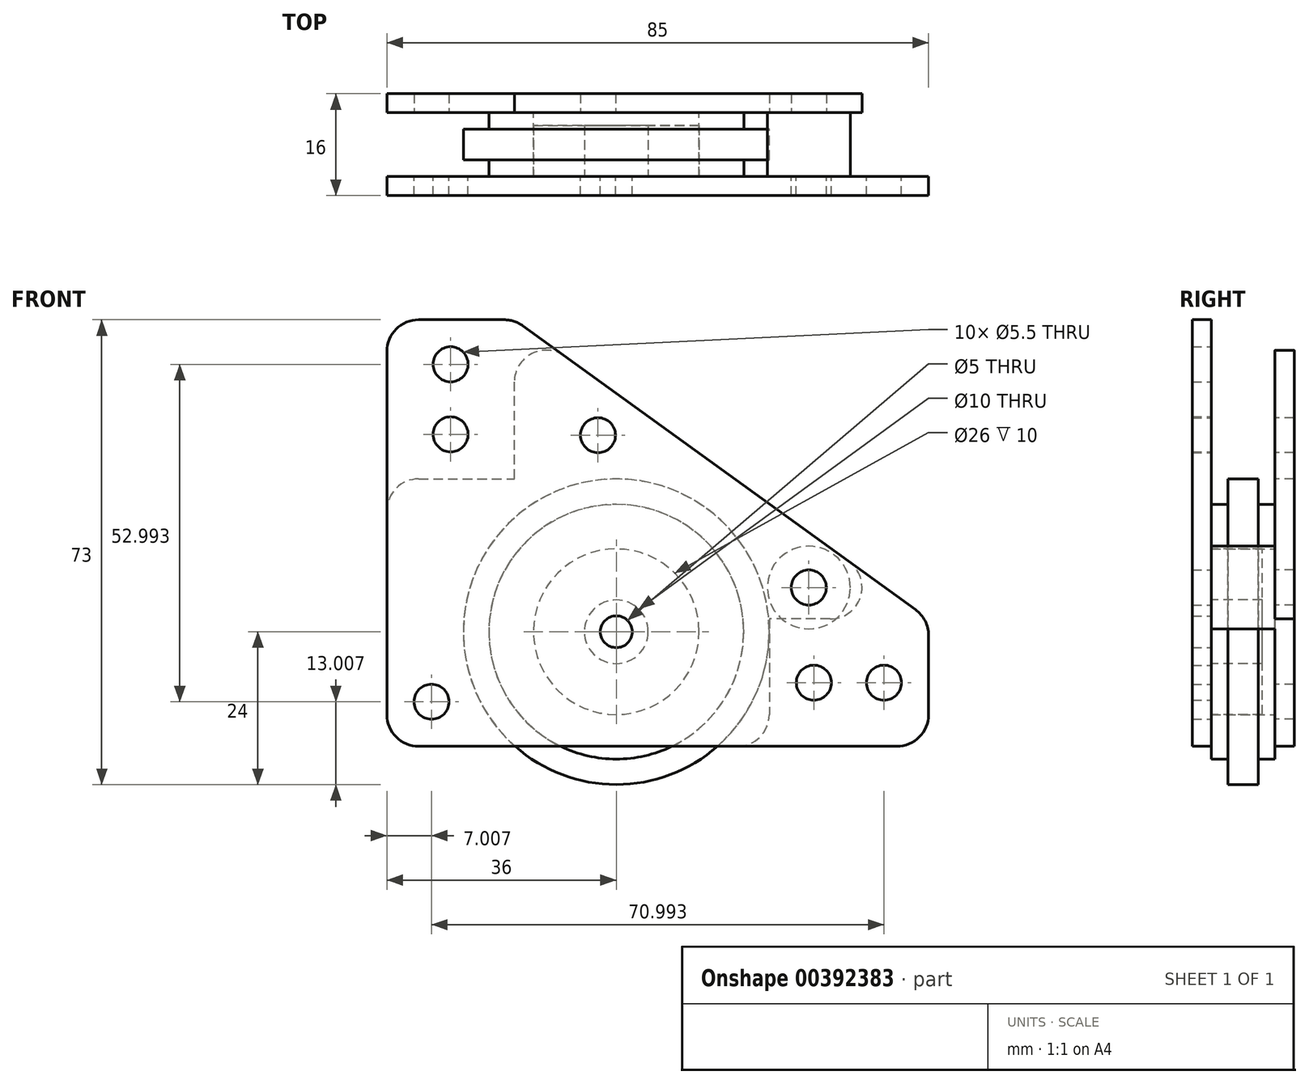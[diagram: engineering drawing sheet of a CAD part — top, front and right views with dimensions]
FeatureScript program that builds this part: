
annotation { "Feature Type Name" : "Feature", "Feature Type Description" : "" }
export const myFeature = defineFeature(function(context is Context, id is Id, definition is map)
    precondition{}
    {
        {
            var Q0;
            Q0=qCreatedBy(makeId("Front.planeOp"),FACE);
            var sketch = newSketch(context, id + "F0", { "sketchPlane" : qUnion([Q0])});
            skCircle(sketch, "E0", {"center": v(0, 0) * mm, "radius": 20 * mm});
            skCircle(sketch, "E1", {"center": v(0, 0) * mm, "radius": 24 * mm});
            skCircle(sketch, "E2", {"center": v(0, 0) * mm, "radius": 13 * mm});
            skSolve(sketch);
        }
        {
            var Q0;
            Q0=makeQuery(id+"F0.imprint","IMPRINT",FACE,{"disambiguationData":[TD([[makeQuery(id+"F0.imprint","IMPRINT",EDGE,{"derivedFrom":sQuery(id+"F0.wireOp",EDGE,"E0")}),1.0]])]});
            var Q1;
            Q1=makeQuery(id+"F0.imprint","IMPRINT",FACE,{"disambiguationData":[TD([[makeQuery(id+"F0.imprint","IMPRINT",EDGE,{"derivedFrom":sQuery(id+"F0.wireOp",EDGE,"E2")}),-1.0]])]});
            var Q2;
            Q2=makeQuery(id+"F0.imprint","IMPRINT",FACE,{"disambiguationData":[TD([[makeQuery(id+"F0.imprint","IMPRINT",EDGE,{"derivedFrom":sQuery(id+"F0.wireOp",EDGE,"ffxK04Et-xQjH-tJyI-gLSu-BGhigi1zAa47")}),-1.0]])]});
            extrude(context, id + "F1", {"entities" : qUnion([Q0, Q1, Q2]), "endBound" : BoundingType.SYMMETRIC, "depth" : 10 * mm});
        }
        {
            var Q0;
            Q0 = qSketchRegion(id + "F0", true);
            extrude(context, id + "F2", {"entities" : qUnion([Q0]), "operationType" : NewBodyOperationType.ADD, "endBound" : BoundingType.SYMMETRIC, "depth" : 4.8 * mm});
        }
        {
            var Q0;
            Q0=makeQuery(id+"F1.opExtrude","CAP_FACE",FACE,{"disambiguationData":[OSD([sQuery(id+"F0.wireOp",EDGE,"E0"),sQuery(id+"F0.wireOp",EDGE,"E2")])],"isStart":false});
            cPlane(context, id + "F3", {"entities" : qUnion([Q0]), "cplaneType" : CPlaneType.OFFSET, "offset" : 0 * mm, "width" : 150 * mm, "height" : 150 * mm});
        }
        {
            var Q0;
            Q0=qCreatedBy(id+"F3.planeOp",FACE);
            var sketch = newSketch(context, id + "F4", { "sketchPlane" : qUnion([Q0])});
            skLineSegment(sketch, "E3", {"start": v(-36, 49) * mm, "end": v(-36, -18) * mm});
            skLineSegment(sketch, "E4", {"start": v(-36, -18) * mm, "end": v(49, -18) * mm});
            skLineSegment(sketch, "E5", {"start": v(49, -18) * mm, "end": v(49, 2) * mm});
            skLineSegment(sketch, "E6", {"start": v(49, 2) * mm, "end": v(-16, 49) * mm});
            skLineSegment(sketch, "E7", {"start": v(-16, 49) * mm, "end": v(-36, 49) * mm});
            skLineSegment(sketch, "E8", {"start": v(49, -8) * mm, "end": v(14.33, -8) * mm, "construction": true});
            skPoint(sketch, "E8.endSnap0", {"position": v(49, -8) * mm});
            skLineSegment(sketch, "E9", {"start": v(-26, 49) * mm, "end": v(-26, 15.47) * mm, "construction": true});
            skCircle(sketch, "E10", {"center": v(-26, 42) * mm, "radius": 2.75 * mm});
            skCircle(sketch, "E11", {"center": v(-26, 31) * mm, "radius": 2.75 * mm});
            skCircle(sketch, "E12", {"center": v(42, -8) * mm, "radius": 2.75 * mm});
            skCircle(sketch, "E13", {"center": v(31, -8) * mm, "radius": 2.75 * mm});
            skCircle(sketch, "E14", {"center": v(-29, -11) * mm, "radius": 7 * mm, "construction": true});
            skCircle(sketch, "E15", {"center": v(-29, -11) * mm, "radius": 2.75 * mm});
            skCircle(sketch, "E16", {"center": v(-2.87, 30.87) * mm, "radius": 7 * mm, "construction": true});
            skCircle(sketch, "E17", {"center": v(30.21, 6.95) * mm, "radius": 7 * mm, "construction": true});
            skCircle(sketch, "E18", {"center": v(-2.87, 30.87) * mm, "radius": 2.75 * mm});
            skCircle(sketch, "E19", {"center": v(30.21, 6.95) * mm, "radius": 2.75 * mm});
            skCircle(sketch, "E20", {"center": v(0, 0) * mm, "radius": 2.5 * mm});
            skSolve(sketch);
        }
        {
            var Q0;
            Q0 = qSketchRegion(id + "F4", true);
            extrude(context, id + "F5", {"entities" : qUnion([Q0]), "depth" : 3 * mm});
        }
        {
            var Q0;
            Q0=qCreatedBy(id+"F3.planeOp",FACE);
            var sketch = newSketch(context, id + "F6", { "sketchPlane" : qUnion([Q0])});
            skCircle(sketch, "E21", {"center": v(0, 0) * mm, "radius": 13 * mm});
            skCircle(sketch, "E22", {"center": v(0, 0) * mm, "radius": 5 * mm});
            skSolve(sketch);
        }
        {
            var Q0;
            Q0 = qSketchRegion(id + "F6", true);
            extrude(context, id + "F7", {"entities" : qUnion([Q0]), "oppositeDirection" : true, "depth" : 8 * mm});
        }
        {
            var Q0;
            Q0=makeQuery(id+"F1.opExtrude","CAP_FACE",FACE,{"disambiguationData":[OSD([sQuery(id+"F0.wireOp",EDGE,"E0"),sQuery(id+"F0.wireOp",EDGE,"E2")])],"isStart":true});
            var sketch = newSketch(context, id + "F8", { "sketchPlane" : qUnion([Q0])});
            skLineSegment(sketch, "E23", {"start": v(-24, -18) * mm, "end": v(36, -18) * mm});
            skLineSegment(sketch, "E24", {"start": v(36, -18) * mm, "end": v(36, 24) * mm});
            skLineSegment(sketch, "E25", {"start": v(36, 24) * mm, "end": v(16, 24) * mm});
            skLineSegment(sketch, "E26", {"start": v(16, 24) * mm, "end": v(16, 49) * mm});
            skLineSegment(sketch, "E27", {"start": v(16, 49) * mm, "end": v(-49, 2) * mm});
            skPoint(sketch, "E28", {"position": v(26, 31) * mm});
            skPoint(sketch, "E29", {"position": v(-31, -8) * mm});
            skPoint(sketch, "E30", {"position": v(-30.21, 6.95) * mm});
            skLineSegment(sketch, "E31", {"start": v(-49, 2) * mm, "end": v(-24, 2) * mm});
            skLineSegment(sketch, "E32", {"start": v(-24, 2) * mm, "end": v(-24, -18) * mm});
            skCircle(sketch, "E33", {"center": v(-30.21, 6.95) * mm, "radius": 2.75 * mm});
            skCircle(sketch, "E34", {"center": v(2.87, 30.87) * mm, "radius": 2.75 * mm});
            skCircle(sketch, "E35", {"center": v(29, -11) * mm, "radius": 2.75 * mm});
            skSolve(sketch);
        }
        {
            var Q0;
            Q0 = qSketchRegion(id + "F8", true);
            extrude(context, id + "F9", {"entities" : qUnion([Q0]), "depth" : 3 * mm});
        }
        {
            var Q0;
            Q0=makeQuery(id+"F9.opExtrude","SWEPT_EDGE",EDGE,{"disambiguationData":[OSD([sQuery(id+"F8.wireOp",EDGE,"E27"),sQuery(id+"F8.wireOp",EDGE,"E31")])]});
            var Q1;
            Q1=makeQuery(id+"F9.opExtrude","SWEPT_EDGE",EDGE,{"disambiguationData":[OSD([sQuery(id+"F8.wireOp",EDGE,"E26"),sQuery(id+"F8.wireOp",EDGE,"E27")])]});
            var Q2;
            Q2=makeQuery(id+"F5.opExtrude","SWEPT_EDGE",EDGE,{"disambiguationData":[OSD([sQuery(id+"F4.wireOp",EDGE,"E3"),sQuery(id+"F4.wireOp",EDGE,"E7")])]});
            var Q3;
            Q3=makeQuery(id+"F5.opExtrude","SWEPT_EDGE",EDGE,{"disambiguationData":[OSD([sQuery(id+"F4.wireOp",EDGE,"E3"),sQuery(id+"F4.wireOp",EDGE,"E4")])]});
            var Q4;
            Q4=makeQuery(id+"F9.opExtrude","SWEPT_EDGE",EDGE,{"disambiguationData":[OSD([sQuery(id+"F8.wireOp",EDGE,"E23"),sQuery(id+"F8.wireOp",EDGE,"E24")])]});
            var Q5;
            Q5=makeQuery(id+"F9.opExtrude","SWEPT_EDGE",EDGE,{"disambiguationData":[OSD([sQuery(id+"F8.wireOp",EDGE,"E24"),sQuery(id+"F8.wireOp",EDGE,"E25")])]});
            var Q6;
            Q6=makeQuery(id+"F9.opExtrude","SWEPT_EDGE",EDGE,{"disambiguationData":[OSD([sQuery(id+"F8.wireOp",EDGE,"E23"),sQuery(id+"F8.wireOp",EDGE,"E32")])]});
            var Q7;
            Q7=makeQuery(id+"F5.opExtrude","SWEPT_EDGE",EDGE,{"disambiguationData":[OSD([sQuery(id+"F4.wireOp",EDGE,"E4"),sQuery(id+"F4.wireOp",EDGE,"E5")])]});
            var Q8;
            Q8=makeQuery(id+"F5.opExtrude","SWEPT_EDGE",EDGE,{"disambiguationData":[OSD([sQuery(id+"F4.wireOp",EDGE,"E5"),sQuery(id+"F4.wireOp",EDGE,"E6")])]});
            var Q9;
            Q9=makeQuery(id+"F5.opExtrude","SWEPT_EDGE",EDGE,{"disambiguationData":[OSD([sQuery(id+"F4.wireOp",EDGE,"E6"),sQuery(id+"F4.wireOp",EDGE,"E7")])]});
            fillet(context, id + "F10", {"entities" : qUnion([Q0, Q1, Q2, Q3, Q4, Q5, Q6, Q7, Q8, Q9]), "radius" : 5 * mm, "tangentPropagation" : true, "allowEdgeOverflow" : false});
        }
        {
            var Q0;
            Q0=makeQuery(id+"F5.opExtrude","CAP_FACE",FACE,{"disambiguationData":[OSD([sQuery(id+"F4.wireOp",EDGE,"E3"),sQuery(id+"F4.wireOp",EDGE,"E4"),sQuery(id+"F4.wireOp",EDGE,"E5"),sQuery(id+"F4.wireOp",EDGE,"E6"),sQuery(id+"F4.wireOp",EDGE,"E7"),sQuery(id+"F4.wireOp",EDGE,"E10"),sQuery(id+"F4.wireOp",EDGE,"E11"),sQuery(id+"F4.wireOp",EDGE,"E12"),sQuery(id+"F4.wireOp",EDGE,"E13"),sQuery(id+"F4.wireOp",EDGE,"E15"),sQuery(id+"F4.wireOp",EDGE,"E18"),sQuery(id+"F4.wireOp",EDGE,"E19"),sQuery(id+"F4.wireOp",EDGE,"E20")])],"isStart":true});
            var sketch = newSketch(context, id + "F11", { "sketchPlane" : qUnion([Q0])});
            skCircle(sketch, "E36", {"center": v(-30.21, 6.95) * mm, "radius": 6.5 * mm});
            skSolve(sketch);
        }
        {
            var Q0;
            Q0 = qSketchRegion(id + "F11", true);
            var Q1;
            Q1=makeQuery(id+"F9.opExtrude","CAP_FACE",FACE,{"disambiguationData":[OSD([sQuery(id+"F8.wireOp",EDGE,"E23"),sQuery(id+"F8.wireOp",EDGE,"E24"),sQuery(id+"F8.wireOp",EDGE,"E25"),sQuery(id+"F8.wireOp",EDGE,"E26"),sQuery(id+"F8.wireOp",EDGE,"E27"),sQuery(id+"F8.wireOp",EDGE,"E31"),sQuery(id+"F8.wireOp",EDGE,"E32"),sQuery(id+"F8.wireOp",EDGE,"E33"),sQuery(id+"F8.wireOp",EDGE,"E34"),sQuery(id+"F8.wireOp",EDGE,"E35")])],"isStart":true});
            extrude(context, id + "F12", {"entities" : qUnion([Q0]), "endBound" : BoundingType.UP_TO_SURFACE, "endBoundEntityFace" : qUnion([Q1]), "depth" : 25 * mm});
        }
    });
